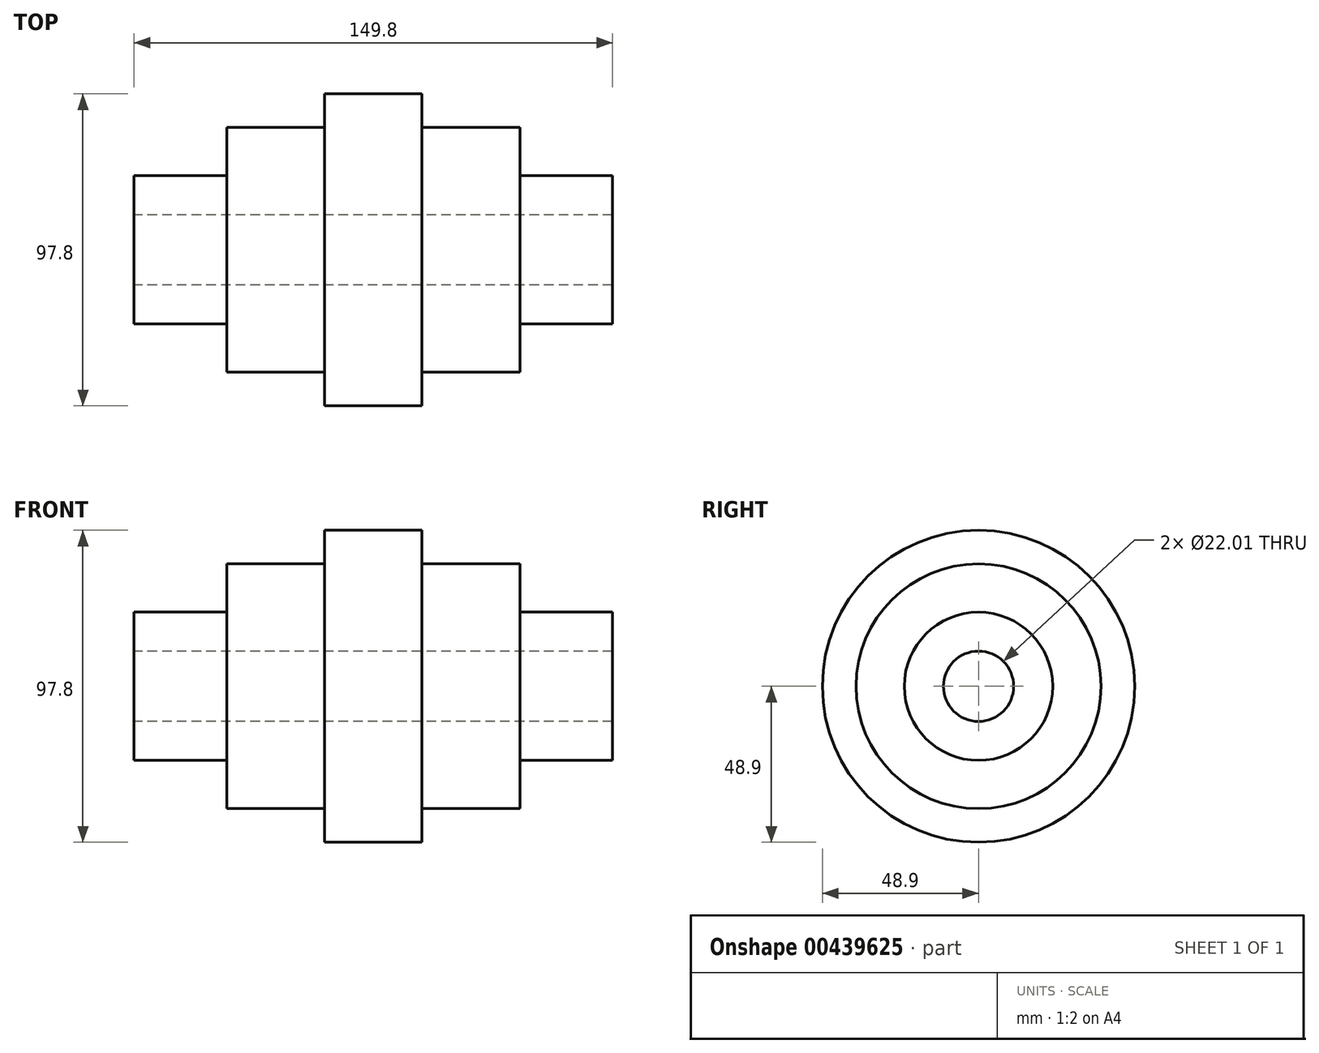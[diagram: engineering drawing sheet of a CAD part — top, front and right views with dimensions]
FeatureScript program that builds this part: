
annotation { "Feature Type Name" : "Feature", "Feature Type Description" : "" }
export const myFeature = defineFeature(function(context is Context, id is Id, definition is map)
    precondition{}
    {
        {
            var Q0;
            Q0=qCreatedBy(makeId("Top.planeOp"),FACE);
            var sketch = newSketch(context, id + "F0", { "sketchPlane" : qUnion([Q0])});
            skLineSegment(sketch, "E0", {"start": v(-75.4, 0) * mm, "end": v(75.11, 0) * mm, "construction": true});
            skLineSegment(sketch, "E1.bottom", {"start": v(45.9, 23.23) * mm, "end": v(74.9, 23.23) * mm});
            skLineSegment(sketch, "E1.top", {"start": v(45.9, 11) * mm, "end": v(74.9, 11) * mm});
            skLineSegment(sketch, "E1.right", {"start": v(74.9, 23.23) * mm, "end": v(74.9, 11) * mm});
            skLineSegment(sketch, "E2.left", {"start": v(45.9, 23.23) * mm, "end": v(45.9, 23.23) * mm});
            skLineSegment(sketch, "E3.top", {"start": v(45.9, 38.35) * mm, "end": v(15.27, 38.35) * mm});
            skLineSegment(sketch, "E3.left", {"start": v(45.9, 23.23) * mm, "end": v(45.9, 38.35) * mm});
            skLineSegment(sketch, "E4.top", {"start": v(15.27, 48.9) * mm, "end": v(0, 48.9) * mm});
            skLineSegment(sketch, "E4.left", {"start": v(15.27, 38.35) * mm, "end": v(15.27, 48.9) * mm});
            skLineSegment(sketch, "E4.right", {"start": v(0, 38.35) * mm, "end": v(0, 48.9) * mm});
            skLineSegment(sketch, "E5", {"start": v(45.9, 11) * mm, "end": v(0, 11) * mm});
            skLineSegment(sketch, "E6", {"start": v(0, 11) * mm, "end": v(0, 38.35) * mm});
            skLineSegment(sketch, "E7.MirrorCS", {"start": v(-15.27, 48.9) * mm, "end": v(0, 48.9) * mm});
            skLineSegment(sketch, "E8.MirrorCS", {"start": v(-15.27, 38.35) * mm, "end": v(-15.27, 48.9) * mm});
            skLineSegment(sketch, "E9.MirrorCS", {"start": v(-45.9, 38.35) * mm, "end": v(-15.27, 38.35) * mm});
            skLineSegment(sketch, "E10.MirrorCS", {"start": v(-45.9, 23.23) * mm, "end": v(-45.9, 38.35) * mm});
            skLineSegment(sketch, "E11.MirrorCS", {"start": v(-45.9, 23.23) * mm, "end": v(-74.9, 23.23) * mm});
            skLineSegment(sketch, "E12.MirrorCS", {"start": v(-74.9, 23.23) * mm, "end": v(-74.9, 11) * mm});
            skLineSegment(sketch, "E13.MirrorCS", {"start": v(-45.9, 11) * mm, "end": v(-74.9, 11) * mm});
            skLineSegment(sketch, "E14.MirrorCS", {"start": v(-45.9, 11) * mm, "end": v(0, 11) * mm});
            skSolve(sketch);
        }
        {
            var Q0;
            Q0=makeQuery(id+"F0.imprint","IMPRINT",FACE,{"disambiguationData":[TD([[makeQuery(id+"F0.imprint","IMPRINT",EDGE,{"derivedFrom":sQuery(id+"F0.wireOp",EDGE,"E1.bottom")}),-1.0]])]});
            var Q1;
            Q1=makeQuery(id+"F0.imprint","IMPRINT",FACE,{"disambiguationData":[TD([[makeQuery(id+"F0.imprint","IMPRINT",EDGE,{"derivedFrom":sQuery(id+"F0.wireOp",EDGE,"E4.right")}),1.0]])]});
            var Q2;
            Q2=sQuery(id+"F0.wireOp",EDGE,"E0");
            revolve(context, id + "F1", {"entities" : qUnion([Q0, Q1]), "axis" : qUnion([Q2]), "revolveType" : RevolveType.FULL});
        }
    });
